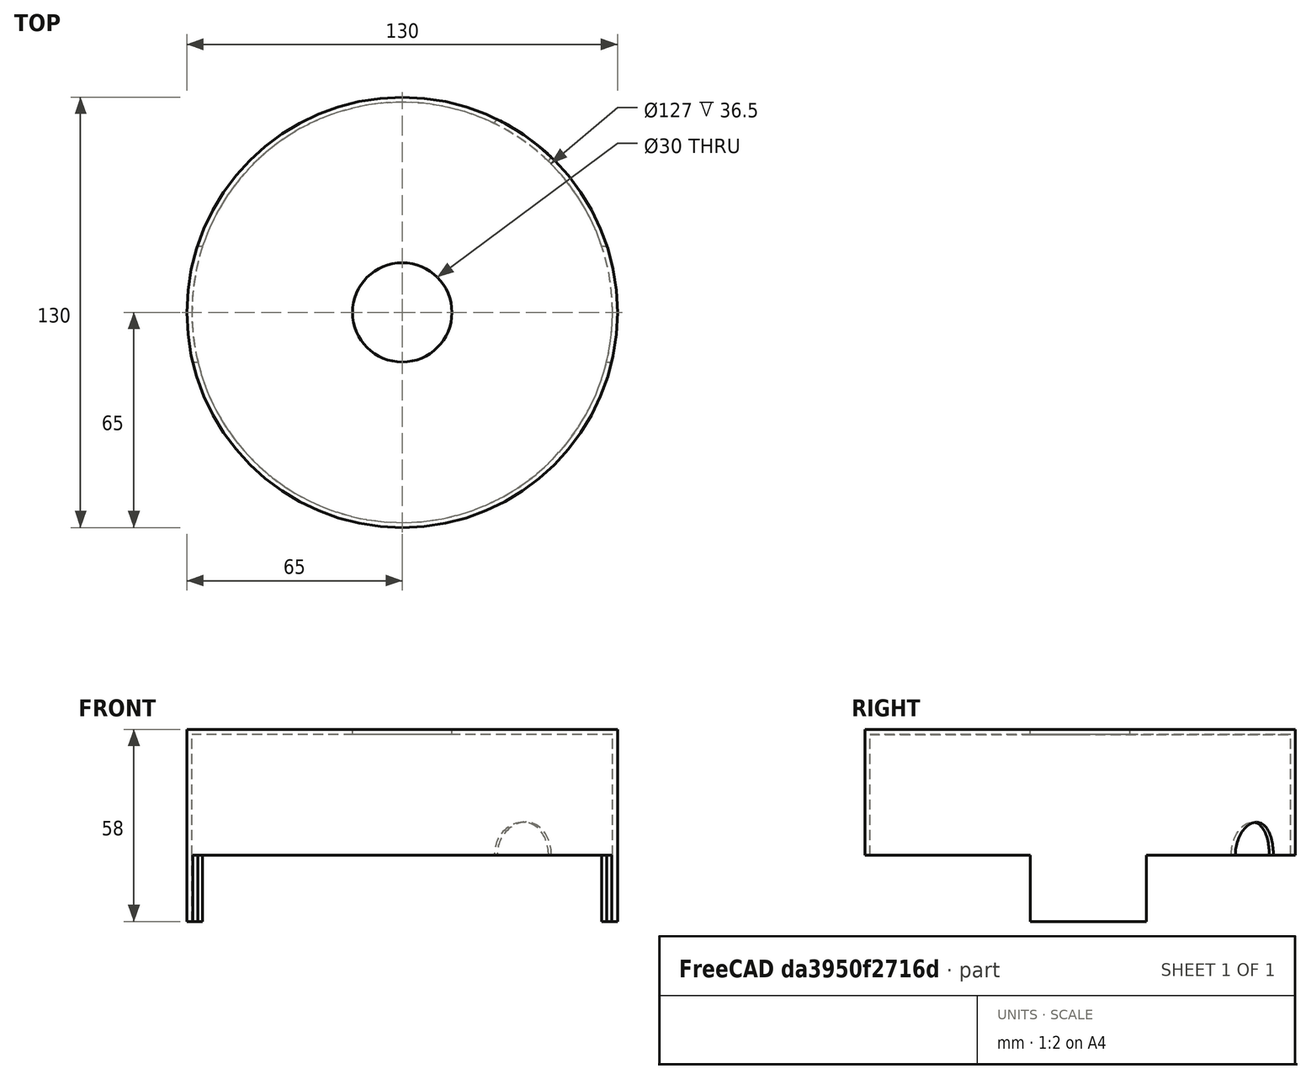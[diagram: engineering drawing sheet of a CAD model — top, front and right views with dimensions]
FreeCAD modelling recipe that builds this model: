
FCSTD DOCUMENT  (FreeCAD 0.15R4671 (Git))
Label: u-sample-stage
License: All rights reserved
LicenseURL: http://en.wikipedia.org/wiki/All_rights_reserved
objects: Part::Cylinder×7, Part::Cut×7, Part::Box×2, Part::MultiFuse×1
note: 17 computed .brp shape members not serialized (recipe doc carries the construction recipe); baked Part::Feature solids carry a one-line shape summary decoded from their .brp

FEATURE [Part::Cylinder] Cylinder  label="Cilindro"
  Angle = 360
  Height = 58
  Radius = 65
FEATURE [Part::Cylinder] Cylinder001  label="Cilindro001"
  Angle = 360
  Height = 56.5
  Radius = 63.5
FEATURE [Part::Cut] Cut
  Base = -> Cylinder
  Tool = -> Cylinder001
FEATURE [Part::Cylinder] Cylinder002  label="Cilindro002"
  Angle = 360
  Height = 20
  Radius = 65
FEATURE [Part::Cut] Cut001
  Base = -> Cut
  Tool = -> Cylinder002
FEATURE [Part::Cylinder] Cylinder003  label="Cilindro003"
  Angle = 360
  Height = 20
  Radius = 65
FEATURE [Part::Cylinder] Cylinder004  label="Cilindro004"
  Angle = 360
  Height = 20
  Radius = 63.5
FEATURE [Part::Cut] Cut002
  Base = -> Cylinder003
  Tool = -> Cylinder004
FEATURE [Part::Box] Box  label="Cubo"
  Height = 20
  Length = 140
  Placement = pos=(-70,20,0) rot=(0,0,1;0rad)
  Width = 70
FEATURE [Part::Box] Box001  label="Cubo001"
  Height = 20
  Length = 140
  Placement = pos=(-70,-85,0) rot=(0,0,1;0rad)
  Width = 70
FEATURE [Part::Cylinder] Cylinder006  label="Cilindro006"
  Angle = 360
  Height = 65
  Radius = 15
FEATURE [Part::Cut] Cut008
  Base = -> Cut002
  Tool = -> Box
FEATURE [Part::Cut] Cut009
  Base = -> Cut008
  Tool = -> Box001
FEATURE [Part::Cut] Cut010
  Base = -> Cut001
  Tool = -> Cylinder006
FEATURE [Part::Cylinder] Cylinder007  label="Cilindro007"
  Angle = 360
  Height = 80
  Placement = pos=(0,0,20) rot=(-0.913318,0.287968,-0.287968;1.66134rad)
  Radius = 10
FEATURE [Part::Cut] Cut011
  Base = -> Cut010
  Tool = -> Cylinder007
FEATURE [Part::MultiFuse] Fusion
  Shapes = -> [Cut009,Cut011]
